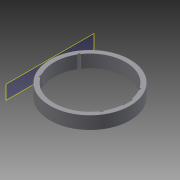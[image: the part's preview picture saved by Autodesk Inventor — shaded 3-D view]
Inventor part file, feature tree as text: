
AUTODESK INVENTOR PART (.ipt)
format: ipt  version: 2014 (Build 180170000, 170)  size: 488,448 bytes
history: native  units: mm
features: reference x4, plane x3, sketch x2, extrude x1, other x1
ambient origin geometry x8: Origin, YZ Plane, XZ Plane, XY Plane, X Axis, Y Axis, Z Axis, Center Point
bodies: Body1 (feature_tree)
feature tree (11):
  plane  "Arbeitsebene1"
  extrude  "Extrusion3"  Depth=6.0mm
  plane  "Work Plane3"
  other  "Prägen1"
  sketch  "Skizze1"  dims[d1=110.0mm d2=6.0mm]
  reference  "Referenz1"
  reference  "Referenz2"
  reference  "Referenz3"
  reference  "Referenz4"
  plane  "Work Plane2"
  sketch  "Sketch2"  dims[d7=15.0mm d8=0.0mm d9=3.0mm d10=0.0mm]
